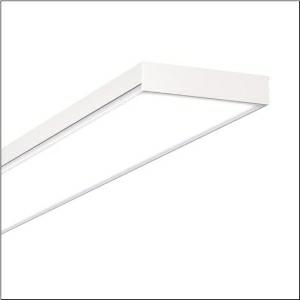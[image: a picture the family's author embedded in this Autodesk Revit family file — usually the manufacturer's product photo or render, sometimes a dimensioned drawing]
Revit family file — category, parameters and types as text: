
# Revit family: apollon_r__31_surface_51mp25wd2441wa_afb6
name_source: partatom
category: Lighting Fixtures
units: mm (PartAtom-declared; Revit-internal decimal feet)

## family parameters
Cut with Voids When Loaded = No
Host = Face
Light Source = No
Part Type = Normal
Room Calculation Point = No
Round Connector Dimension = Use Diameter
Shared = No

## types (1)
- Apollon® 31 Surface (1 x LED, 3800 lm, 28 W, 4000K)
    Apparent Load = 28 VA
    CIE Flux Codes = 61 87 97 97 100
    Color Rendering = 80
    Color Temperature = 4000K
    Default Elevation = 1800 mm
    Description = Apollon® 31 Surface, office luminaire, primary optical cover: micro prismatic cover, of PMMA, light emission: direct distribution, primary light characteristic: symmetric, installation type: surface-mounted, LED, rated luminous flux: 3.800lm, luminous efficacy: 134lm/W, light colour: 840, colour temperature: 4000K, control gear: DALI 2, with terminal, 5-pole, mains connection: 220..240V, AC, 50/60Hz, rated input power: 28W, housing, of sheet steel, coil coated, traffic white (RAL 9016), length: 1.245mm, width: 200mm, height: 44mm, protection rating (complete): IP20, insulation class (complete): insulation class II (safety insulation), certification: CE, impact resistance: IK02, permissible operating ambient temperature: -20..+40°C, standard: EN 60598-2-22, packaging unit: 1 piece
    Height = 44 mm
    Lamp = 1 x LED
    Lamp Light Flux = 3800 lm
    Lamp Power = 28 W
    Lamp count = 1
    Length = 1245 mm
    Luminous efficacy = 136 lm/W
    Manufacturer = Siteco
    ModVariant = No
    Model = 51MP25WD2441WA
    Mounting Place = Ceiling
    Mounting Type = Surface mounted
    Number of Poles = 1
    OnlyDefault = Yes
    Power Factor = 1
    Product Name = Apollon® 31 Surface
    Product group = office luminaire | ceiling mounted
    ProductGroupID = 302
    Protection Class = Protection class II
    Protection Degree = IP 20
    RLX_Detail_Level = 1
    RLX_Emergency_Light_Flux = 0 lm
    RLX_Emergency_Type = 0
    RLX_Emergency_Type_DB = No
    RlxData = <blob elided: 20737 chars, md5=167a96d8>
    Socket = socket
    Standby Power = 0 W
    System Light Flux = 3800 lm
    System Power = 28 W
    Type Comments = Product without accessories
    Type Image = l_1313658.jpg
    URL = http://relux.com
    VarID = ---
    Voltage = 0 V
    Weight = 0.00 kg
    Width = 200 mm  [stored 0.656168 ft]

note: [stored X ft] marks values corroborated as IEEE doubles in the binary element streams (Revit-internal decimal feet)

## geometry (parser evidence)
native form markers: Blend x4, Sweep x10
no freeform markers — native parametric forms only
